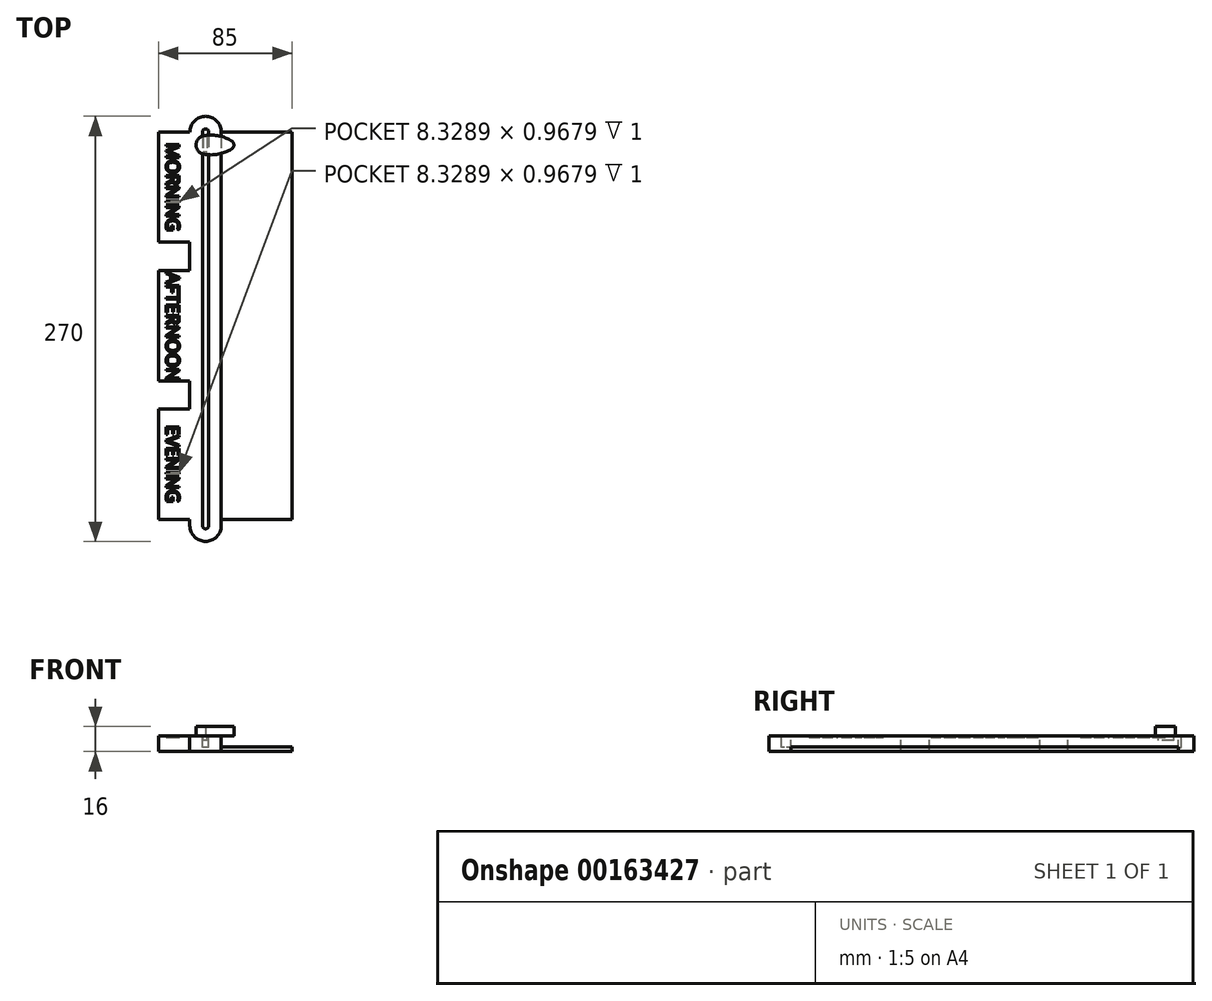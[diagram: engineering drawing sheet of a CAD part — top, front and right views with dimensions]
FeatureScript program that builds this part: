
annotation { "Feature Type Name" : "Feature", "Feature Type Description" : "" }
export const myFeature = defineFeature(function(context is Context, id is Id, definition is map)
    precondition{}
    {
        {
            var Q0;
            Q0=qCreatedBy(makeId("Top.planeOp"),FACE);
            var sketch = newSketch(context, id + "F0", { "sketchPlane" : qUnion([Q0])});
            skLineSegment(sketch, "E0.left", {"start": v(-10, 125) * mm, "end": v(-10, -125) * mm});
            skLineSegment(sketch, "E0.right", {"start": v(10, 125) * mm, "end": v(10, -125) * mm});
            skPoint(sketch, "E0.middle", {"position": v(0, 0) * mm});
            skArc(sketch, "E1", {"start": v(10, 125) * mm, "mid": v(0, 135) * mm, "end": v(-10, 125) * mm});
            skArc(sketch, "E2", {"start": v(-10, -125) * mm, "mid": v(0, -135) * mm, "end": v(10, -125) * mm});
            skLineSegment(sketch, "E3", {"start": v(0, 135) * mm, "end": v(0, -135) * mm, "construction": true});
            skSolve(sketch);
        }
        {
            var Q0;
            Q0 = qSketchRegion(id + "F0", true);
            extrude(context, id + "F1", {"entities" : qUnion([Q0]), "oppositeDirection" : true, "depth" : 10 * mm});
        }
        {
            var Q0;
            Q0=makeQuery(id+"F1.opExtrude","CAP_FACE",FACE,{"disambiguationData":[OSD([sQuery(id+"F0.wireOp",EDGE,"E0.left"),sQuery(id+"F0.wireOp",EDGE,"E0.right"),sQuery(id+"F0.wireOp",EDGE,"E1"),sQuery(id+"F0.wireOp",EDGE,"E2")])],"isStart":true});
            var sketch = newSketch(context, id + "F2", { "sketchPlane" : qUnion([Q0])});
            skLineSegment(sketch, "E4.bottom", {"start": v(-10, 125) * mm, "end": v(-30, 125) * mm});
            skLineSegment(sketch, "E4.top", {"start": v(-10, 55) * mm, "end": v(-30, 55) * mm});
            skLineSegment(sketch, "E4.left", {"start": v(-10, 125) * mm, "end": v(-10, 55) * mm});
            skLineSegment(sketch, "E4.right", {"start": v(-30, 125) * mm, "end": v(-30, 55) * mm});
            skLineSegment(sketch, "E5.0.1.0", {"start": v(-10, -33) * mm, "end": v(-30, -33) * mm});
            skLineSegment(sketch, "E5.0.1.1", {"start": v(-10, 37) * mm, "end": v(-10, -33) * mm});
            skLineSegment(sketch, "E5.0.1.2", {"start": v(-10, 37) * mm, "end": v(-30, 37) * mm});
            skLineSegment(sketch, "E5.0.1.3", {"start": v(-30, 37) * mm, "end": v(-30, -33) * mm});
            skLineSegment(sketch, "E5.0.2.0", {"start": v(-10, -121) * mm, "end": v(-30, -121) * mm});
            skLineSegment(sketch, "E5.0.2.1", {"start": v(-10, -51) * mm, "end": v(-10, -121) * mm});
            skLineSegment(sketch, "E5.0.2.2", {"start": v(-10, -51) * mm, "end": v(-30, -51) * mm});
            skLineSegment(sketch, "E5.0.2.3", {"start": v(-30, -51) * mm, "end": v(-30, -121) * mm});
            skLineSegment(sketch, "E5.direction1", {"start": v(-30, 55) * mm, "end": v(-5, 55) * mm, "construction": true});
            skLineSegment(sketch, "E5.direction2", {"start": v(-30, 55) * mm, "end": v(-30, -33) * mm, "construction": true});
            skSolve(sketch);
        }
        {
            var Q0;
            Q0 = qSketchRegion(id + "F2", true);
            var Q1;
            Q1=makeQuery(id+"F1.opExtrude","CAP_FACE",FACE,{"disambiguationData":[OSD([sQuery(id+"F0.wireOp",EDGE,"E0.left"),sQuery(id+"F0.wireOp",EDGE,"E0.right"),sQuery(id+"F0.wireOp",EDGE,"E1"),sQuery(id+"F0.wireOp",EDGE,"E2")])],"isStart":false});
            extrude(context, id + "F3", {"entities" : qUnion([Q0]), "operationType" : NewBodyOperationType.ADD, "endBound" : BoundingType.UP_TO_SURFACE, "oppositeDirection" : true, "endBoundEntityFace" : qUnion([Q1]), "depth" : 25 * mm});
        }
        {
            var Q0;
            Q0=makeQuery(id+"F3.boolean.opBoolean","MERGE",FACE,{"derivedFrom":[makeQuery(id+"F1.opExtrude","CAP_FACE",FACE,{"disambiguationData":[OSD([sQuery(id+"F0.wireOp",EDGE,"E0.left"),sQuery(id+"F0.wireOp",EDGE,"E0.right"),sQuery(id+"F0.wireOp",EDGE,"E1"),sQuery(id+"F0.wireOp",EDGE,"E2")])],"isStart":true}),makeQuery(id+"F3.opExtrude","CAP_FACE",FACE,{"disambiguationData":[OSD([sQuery(id+"F2.wireOp",EDGE,"E4.bottom"),sQuery(id+"F2.wireOp",EDGE,"E4.top"),sQuery(id+"F2.wireOp",EDGE,"E4.left"),sQuery(id+"F2.wireOp",EDGE,"E4.right")])],"isStart":true}),makeQuery(id+"F3.opExtrude","CAP_FACE",FACE,{"disambiguationData":[OSD([sQuery(id+"F2.wireOp",EDGE,"E5.0.1.0"),sQuery(id+"F2.wireOp",EDGE,"E5.0.1.1"),sQuery(id+"F2.wireOp",EDGE,"E5.0.1.2"),sQuery(id+"F2.wireOp",EDGE,"E5.0.1.3")])],"isStart":true}),makeQuery(id+"F3.opExtrude","CAP_FACE",FACE,{"disambiguationData":[OSD([sQuery(id+"F2.wireOp",EDGE,"E5.0.2.0"),sQuery(id+"F2.wireOp",EDGE,"E5.0.2.1"),sQuery(id+"F2.wireOp",EDGE,"E5.0.2.2"),sQuery(id+"F2.wireOp",EDGE,"E5.0.2.3")])],"isStart":true})]});
            var sketch = newSketch(context, id + "F4", { "sketchPlane" : qUnion([Q0])});
            skLineSegment(sketch, "E6", {"start": v(0, 135) * mm, "end": v(0, 116.81) * mm});
            skCircle(sketch, "E7", {"center": v(0, 116.81) * mm, "radius": 6 * mm});
            skCircle(sketch, "E8", {"center": v(15, 116.81) * mm, "radius": 3 * mm});
            skArc(sketch, "E9", {"start": v(16.55, 119.38) * mm, "mid": v(8.08, 122.63) * mm, "end": v(-1, 122.73) * mm});
            skLineSegment(sketch, "E10", {"start": v(0, 116.81) * mm, "end": v(15, 116.81) * mm});
            skArc(sketch, "E11.MirrorCS", {"start": v(16.55, 114.24) * mm, "mid": v(8.08, 111) * mm, "end": v(-1, 110.9) * mm});
            skSolve(sketch);
        }
        {
            var Q0;
            {var subQ3=sQuery(id+"F4.wireOp",EDGE,"E10");var subQ5=sQuery(id+"F4.wireOp",EDGE,"E6");var subQ7=makeQuery(id+"F4.imprint","INTERSECT",VERTEX,{"derivedFrom":[subQ5,subQ3]});Q0=makeQuery(id+"F4.imprint","IMPRINT",FACE,{"disambiguationData":[TD([[makeQuery(id+"F4.imprint","IMPRINT",EDGE,{"disambiguationData":[TD([[subQ7,1.0]])],"derivedFrom":subQ5}),-1.0]])]});}
            var Q1;
            {var subQ0=sQuery(id+"F4.wireOp",EDGE,"E10");var subQ1=sQuery(id+"F4.wireOp",EDGE,"E6");var subQ2=makeQuery(id+"F4.imprint","INTERSECT",VERTEX,{"derivedFrom":[subQ1,subQ0]});Q1=makeQuery(id+"F4.imprint","IMPRINT",FACE,{"disambiguationData":[TD([[makeQuery(id+"F4.imprint","IMPRINT",EDGE,{"disambiguationData":[TD([[subQ2,1.0]])],"derivedFrom":subQ1}),1.0]])]});}
            var Q2;
            {var subQ5=sQuery(id+"F4.wireOp",EDGE,"E9");var subQ6=sQuery(id+"F4.wireOp",EDGE,"E6");var subQ7=makeQuery(id+"F4.imprint","INTERSECT",VERTEX,{"derivedFrom":[subQ6,subQ5]});Q2=makeQuery(id+"F4.imprint","IMPRINT",FACE,{"disambiguationData":[TD([[makeQuery(id+"F4.imprint","IMPRINT",EDGE,{"disambiguationData":[TD([[subQ7,-1.0]])],"derivedFrom":subQ6}),1.0]])]});}
            var Q3;
            {var subQ0=sQuery(id+"F4.wireOp",EDGE,"E9");var subQ1=sQuery(id+"F4.wireOp",EDGE,"E8");var subQ2=makeQuery(id+"F4.imprint","INTERSECT",VERTEX,{"derivedFrom":[subQ1,subQ0]});Q3=makeQuery(id+"F4.imprint","IMPRINT",FACE,{"disambiguationData":[TD([[makeQuery(id+"F4.imprint","IMPRINT",EDGE,{"disambiguationData":[TD([[subQ2,-1.0]])],"derivedFrom":subQ1}),-1.0]])]});}
            var Q4;
            {var subQ0=sQuery(id+"F4.wireOp",EDGE,"E8");var subQ1=makeQuery(id+"F4.imprint","INTERSECT",VERTEX,{"derivedFrom":[subQ0,sQuery(id+"F4.wireOp",EDGE,"E9")]});Q4=makeQuery(id+"F4.imprint","IMPRINT",FACE,{"disambiguationData":[TD([[makeQuery(id+"F4.imprint","IMPRINT",EDGE,{"disambiguationData":[TD([[subQ1,-1.0]])],"derivedFrom":subQ0}),1.0]])]});}
            var Q5;
            {var subQ0=sQuery(id+"F4.wireOp",EDGE,"E11.MirrorCS");var subQ1=sQuery(id+"F4.wireOp",EDGE,"E8");var subQ2=makeQuery(id+"F4.imprint","INTERSECT",VERTEX,{"derivedFrom":[subQ1,subQ0]});Q5=makeQuery(id+"F4.imprint","IMPRINT",FACE,{"disambiguationData":[TD([[makeQuery(id+"F4.imprint","IMPRINT",EDGE,{"disambiguationData":[TD([[subQ2,1.0]])],"derivedFrom":subQ1}),-1.0]])]});}
            var Q6;
            {var subQ0=sQuery(id+"F4.wireOp",EDGE,"E11.MirrorCS");var subQ1=sQuery(id+"F4.wireOp",EDGE,"E7");var subQ2=makeQuery(id+"F4.imprint","INTERSECT",VERTEX,{"derivedFrom":[subQ1,subQ0]});Q6=makeQuery(id+"F4.imprint","IMPRINT",FACE,{"disambiguationData":[TD([[makeQuery(id+"F4.imprint","IMPRINT",EDGE,{"disambiguationData":[TD([[subQ2,-1.0]])],"derivedFrom":subQ1}),-1.0]])]});}
            extrude(context, id + "F5", {"entities" : qUnion([Q0, Q1, Q2, Q3, Q4, Q5, Q6]), "depth" : 6 * mm});
        }
        {
            var Q0;
            {var subQ0=sQuery(id+"F0.wireOp",EDGE,"E2");var subQ1=sQuery(id+"F0.wireOp",EDGE,"E1");var subQ2=sQuery(id+"F0.wireOp",EDGE,"E0.right");var subQ3=sQuery(id+"F0.wireOp",EDGE,"E0.left");Q0=makeQuery(id+"F3.boolean.opBoolean","MERGE",FACE,{"derivedFrom":[makeQuery(id+"F1.opExtrude","CAP_FACE",FACE,{"disambiguationData":[OSD([subQ3,subQ2,subQ1,subQ0])],"isStart":false}),makeQuery(id+"F3.opExtrude","CAP_FACE",FACE,{"disambiguationData":[OSD([subQ3,subQ2,subQ1,subQ0]),ownerDisambiguation([makeQuery(id+"F3.opExtrude","SWEPT_BODY",BODY,{"disambiguationData":[OSD([sQuery(id+"F2.wireOp",EDGE,"E4.bottom"),sQuery(id+"F2.wireOp",EDGE,"E4.top"),sQuery(id+"F2.wireOp",EDGE,"E4.left"),sQuery(id+"F2.wireOp",EDGE,"E4.right")])]})])],"isStart":false}),makeQuery(id+"F3.opExtrude","CAP_FACE",FACE,{"disambiguationData":[OSD([subQ3,subQ2,subQ1,subQ0]),ownerDisambiguation([makeQuery(id+"F3.opExtrude","SWEPT_BODY",BODY,{"disambiguationData":[OSD([sQuery(id+"F2.wireOp",EDGE,"E5.0.1.0"),sQuery(id+"F2.wireOp",EDGE,"E5.0.1.1"),sQuery(id+"F2.wireOp",EDGE,"E5.0.1.2"),sQuery(id+"F2.wireOp",EDGE,"E5.0.1.3")])]})])],"isStart":false}),makeQuery(id+"F3.opExtrude","CAP_FACE",FACE,{"disambiguationData":[OSD([subQ3,subQ2,subQ1,subQ0]),ownerDisambiguation([makeQuery(id+"F3.opExtrude","SWEPT_BODY",BODY,{"disambiguationData":[OSD([sQuery(id+"F2.wireOp",EDGE,"E5.0.2.0"),sQuery(id+"F2.wireOp",EDGE,"E5.0.2.1"),sQuery(id+"F2.wireOp",EDGE,"E5.0.2.2"),sQuery(id+"F2.wireOp",EDGE,"E5.0.2.3")])]})])],"isStart":false})]});}
            var sketch = newSketch(context, id + "F6", { "sketchPlane" : qUnion([Q0])});
            skLineSegment(sketch, "E12.bottom", {"start": v(10, 121) * mm, "end": v(55, 121) * mm});
            skLineSegment(sketch, "E12.top", {"start": v(10, -125) * mm, "end": v(55, -125) * mm});
            skLineSegment(sketch, "E12.left", {"start": v(10, 121) * mm, "end": v(10, -125) * mm});
            skLineSegment(sketch, "E12.right", {"start": v(55, 121) * mm, "end": v(55, -125) * mm});
            skSolve(sketch);
        }
        {
            var Q0;
            Q0=makeQuery(id+"F6.imprint","IMPRINT",FACE,{"disambiguationData":[TD([[makeQuery(id+"F6.imprint","IMPRINT",EDGE,{"derivedFrom":sQuery(id+"F6.wireOp",EDGE,"E12.bottom")}),-1.0]])]});
            extrude(context, id + "F7", {"entities" : qUnion([Q0]), "operationType" : NewBodyOperationType.ADD, "oppositeDirection" : true, "depth" : 3 * mm});
        }
        {
            var Q0;
            Q0=makeQuery(id+"F3.boolean.opBoolean","MERGE",FACE,{"derivedFrom":[makeQuery(id+"F1.opExtrude","CAP_FACE",FACE,{"disambiguationData":[OSD([sQuery(id+"F0.wireOp",EDGE,"E0.left"),sQuery(id+"F0.wireOp",EDGE,"E0.right"),sQuery(id+"F0.wireOp",EDGE,"E1"),sQuery(id+"F0.wireOp",EDGE,"E2")])],"isStart":true}),makeQuery(id+"F3.opExtrude","CAP_FACE",FACE,{"disambiguationData":[OSD([sQuery(id+"F2.wireOp",EDGE,"E4.bottom"),sQuery(id+"F2.wireOp",EDGE,"E4.top"),sQuery(id+"F2.wireOp",EDGE,"E4.left"),sQuery(id+"F2.wireOp",EDGE,"E4.right")])],"isStart":true}),makeQuery(id+"F3.opExtrude","CAP_FACE",FACE,{"disambiguationData":[OSD([sQuery(id+"F2.wireOp",EDGE,"E5.0.1.0"),sQuery(id+"F2.wireOp",EDGE,"E5.0.1.1"),sQuery(id+"F2.wireOp",EDGE,"E5.0.1.2"),sQuery(id+"F2.wireOp",EDGE,"E5.0.1.3")])],"isStart":true}),makeQuery(id+"F3.opExtrude","CAP_FACE",FACE,{"disambiguationData":[OSD([sQuery(id+"F2.wireOp",EDGE,"E5.0.2.0"),sQuery(id+"F2.wireOp",EDGE,"E5.0.2.1"),sQuery(id+"F2.wireOp",EDGE,"E5.0.2.2"),sQuery(id+"F2.wireOp",EDGE,"E5.0.2.3")])],"isStart":true})]});
            var sketch = newSketch(context, id + "F8", { "sketchPlane" : qUnion([Q0])});
            skSolve(sketch);
        }
        {
            var Q0;
            {var subQ4=sQuery(id+"F0.wireOp",EDGE,"E0.right");Q0=makeQuery(id+"F8.imprint","IMPRINT",FACE,{"disambiguationData":[TD([[makeQuery(id+"F8.imprint","IMPRINT",EDGE,{"derivedFrom":makeQuery(id+"F1.opExtrude","CAP_EDGE",EDGE,{"disambiguationData":[OSD([subQ4])],"isStart":true})}),-1.0]])]});}
            var sketch = newSketch(context, id + "F9", { "sketchPlane" : qUnion([Q0])});
            skLineSegment(sketch, "E13", {"start": v(0, 125) * mm, "end": v(0, -125) * mm});
            skArc(sketch, "E14.0.startCap", {"start": v(-2, 125) * mm, "mid": v(0, 127) * mm, "end": v(2, 125) * mm});
            skArc(sketch, "E14.0.endCap", {"start": v(2, -125) * mm, "mid": v(0, -127) * mm, "end": v(-2, -125) * mm});
            skLineSegment(sketch, "E14.0.left", {"start": v(2, 125) * mm, "end": v(2, -125) * mm});
            skLineSegment(sketch, "E14.0.right", {"start": v(-2, 125) * mm, "end": v(-2, -125) * mm});
            skSolve(sketch);
        }
        {
            var Q0;
            Q0 = qSketchRegion(id + "F9", true);
            extrude(context, id + "F10", {"entities" : qUnion([Q0]), "operationType" : NewBodyOperationType.REMOVE, "oppositeDirection" : true, "depth" : 25 * mm});
        }
        {
            var Q0;
            {var subQ4=sQuery(id+"F0.wireOp",EDGE,"E0.right");Q0=makeQuery(id+"F8.imprint","IMPRINT",FACE,{"disambiguationData":[TD([[makeQuery(id+"F8.imprint","IMPRINT",EDGE,{"derivedFrom":makeQuery(id+"F1.opExtrude","CAP_EDGE",EDGE,{"disambiguationData":[OSD([subQ4])],"isStart":true})}),-1.0]])]});}
            var sketch = newSketch(context, id + "F11", { "sketchPlane" : qUnion([Q0])});
            skLineSegment(sketch, "E15.bottom", {"start": v(1.1, 122.2) * mm, "end": v(-1.55, 122.2) * mm});
            skLineSegment(sketch, "E15.top", {"start": v(1.1, 112.27) * mm, "end": v(-1.55, 112.27) * mm});
            skLineSegment(sketch, "E15.left", {"start": v(1.1, 122.2) * mm, "end": v(1.1, 112.27) * mm});
            skLineSegment(sketch, "E15.right", {"start": v(-1.55, 122.2) * mm, "end": v(-1.55, 112.27) * mm});
            skSolve(sketch);
        }
        {
            var Q0;
            Q0=makeQuery(id+"F11.imprint","IMPRINT",FACE,{"disambiguationData":[TD([[makeQuery(id+"F11.imprint","IMPRINT",EDGE,{"derivedFrom":sQuery(id+"F11.wireOp",EDGE,"E15.bottom")}),1.0]])]});
            extrude(context, id + "F12", {"entities" : qUnion([Q0]), "operationType" : NewBodyOperationType.ADD, "oppositeDirection" : true, "depth" : 3 * mm});
        }
        {
            var Q0;
            {var subQ4=sQuery(id+"F0.wireOp",EDGE,"E0.right");Q0=makeQuery(id+"F8.imprint","IMPRINT",FACE,{"disambiguationData":[TD([[makeQuery(id+"F8.imprint","IMPRINT",EDGE,{"derivedFrom":makeQuery(id+"F1.opExtrude","CAP_EDGE",EDGE,{"disambiguationData":[OSD([subQ4])],"isStart":true})}),-1.0]])]});}
            var sketch = newSketch(context, id + "F13", { "sketchPlane" : qUnion([Q0])});
            skText(sketch, "E16", { "text": "MORNING", "fontName": "OpenSans-Regular.ttf"});
            skText(sketch, "E17", { "text": "AFTERNOON", "fontName": "OpenSans-Regular.ttf"});
            skText(sketch, "E18", { "text": "EVENING", "fontName": "OpenSans-Regular.ttf"});
            const initialGuessF13  = {"E16": [-0.025, 0.11807, 0, -1, 0.0084], "E17": [-0.025, 0.036, 0, -1, 0.0084], "E18": [-0.025, -0.06127, 0, -1, 0.0084]};
            skSetInitialGuess(sketch, initialGuessF13);
            skSolve(sketch);
        }
        {
            var Q0;
            Q0 = qSketchRegion(id + "F13", true);
            extrude(context, id + "F14", {"entities" : qUnion([Q0]), "operationType" : NewBodyOperationType.REMOVE, "oppositeDirection" : true, "depth" : 1 * mm});
        }
        {
            var Q0;
            {var subQ0=sQuery(id+"F0.wireOp",EDGE,"E2");var subQ1=sQuery(id+"F0.wireOp",EDGE,"E1");var subQ2=sQuery(id+"F0.wireOp",EDGE,"E0.right");var subQ3=sQuery(id+"F0.wireOp",EDGE,"E0.left");Q0=makeQuery(id+"F7.boolean.opBoolean","MERGE",FACE,{"derivedFrom":[makeQuery(id+"F3.boolean.opBoolean","MERGE",FACE,{"derivedFrom":[makeQuery(id+"F1.opExtrude","CAP_FACE",FACE,{"disambiguationData":[OSD([subQ3,subQ2,subQ1,subQ0])],"isStart":false}),makeQuery(id+"F3.opExtrude","CAP_FACE",FACE,{"disambiguationData":[OSD([subQ3,subQ2,subQ1,subQ0]),ownerDisambiguation([makeQuery(id+"F3.opExtrude","SWEPT_BODY",BODY,{"disambiguationData":[OSD([sQuery(id+"F2.wireOp",EDGE,"E4.bottom"),sQuery(id+"F2.wireOp",EDGE,"E4.top"),sQuery(id+"F2.wireOp",EDGE,"E4.left"),sQuery(id+"F2.wireOp",EDGE,"E4.right")])]})])],"isStart":false}),makeQuery(id+"F3.opExtrude","CAP_FACE",FACE,{"disambiguationData":[OSD([subQ3,subQ2,subQ1,subQ0]),ownerDisambiguation([makeQuery(id+"F3.opExtrude","SWEPT_BODY",BODY,{"disambiguationData":[OSD([sQuery(id+"F2.wireOp",EDGE,"E5.0.1.0"),sQuery(id+"F2.wireOp",EDGE,"E5.0.1.1"),sQuery(id+"F2.wireOp",EDGE,"E5.0.1.2"),sQuery(id+"F2.wireOp",EDGE,"E5.0.1.3")])]})])],"isStart":false}),makeQuery(id+"F3.opExtrude","CAP_FACE",FACE,{"disambiguationData":[OSD([subQ3,subQ2,subQ1,subQ0]),ownerDisambiguation([makeQuery(id+"F3.opExtrude","SWEPT_BODY",BODY,{"disambiguationData":[OSD([sQuery(id+"F2.wireOp",EDGE,"E5.0.2.0"),sQuery(id+"F2.wireOp",EDGE,"E5.0.2.1"),sQuery(id+"F2.wireOp",EDGE,"E5.0.2.2"),sQuery(id+"F2.wireOp",EDGE,"E5.0.2.3")])]})])],"isStart":false})]}),makeQuery(id+"F7.opExtrude","CAP_FACE",FACE,{"disambiguationData":[OSD([sQuery(id+"F6.wireOp",EDGE,"E12.bottom"),sQuery(id+"F6.wireOp",EDGE,"E12.top"),sQuery(id+"F6.wireOp",EDGE,"E12.left"),sQuery(id+"F6.wireOp",EDGE,"E12.right")])],"isStart":true})]});}
            var sketch = newSketch(context, id + "F15", { "sketchPlane" : qUnion([Q0])});
            skLineSegment(sketch, "E19.0", {"start": v(2, -125) * mm, "end": v(2, 125) * mm});
            skPoint(sketch, "E20.0", {"position": v(0, 127) * mm});
            skLineSegment(sketch, "E21.0", {"start": v(-2, -125) * mm, "end": v(-2, 125) * mm});
            skArc(sketch, "E22.0", {"start": v(2, 125) * mm, "mid": v(0, 127) * mm, "end": v(-2, 125) * mm});
            skArc(sketch, "E23.0", {"start": v(-2, -125) * mm, "mid": v(0, -127) * mm, "end": v(2, -125) * mm});
            skSolve(sketch);
        }
        {
            var Q0;
            Q0 = qSketchRegion(id + "F15", true);
            extrude(context, id + "F16", {"entities" : qUnion([Q0]), "operationType" : NewBodyOperationType.ADD, "oppositeDirection" : true, "depth" : 2.5 * mm});
        }
    });
